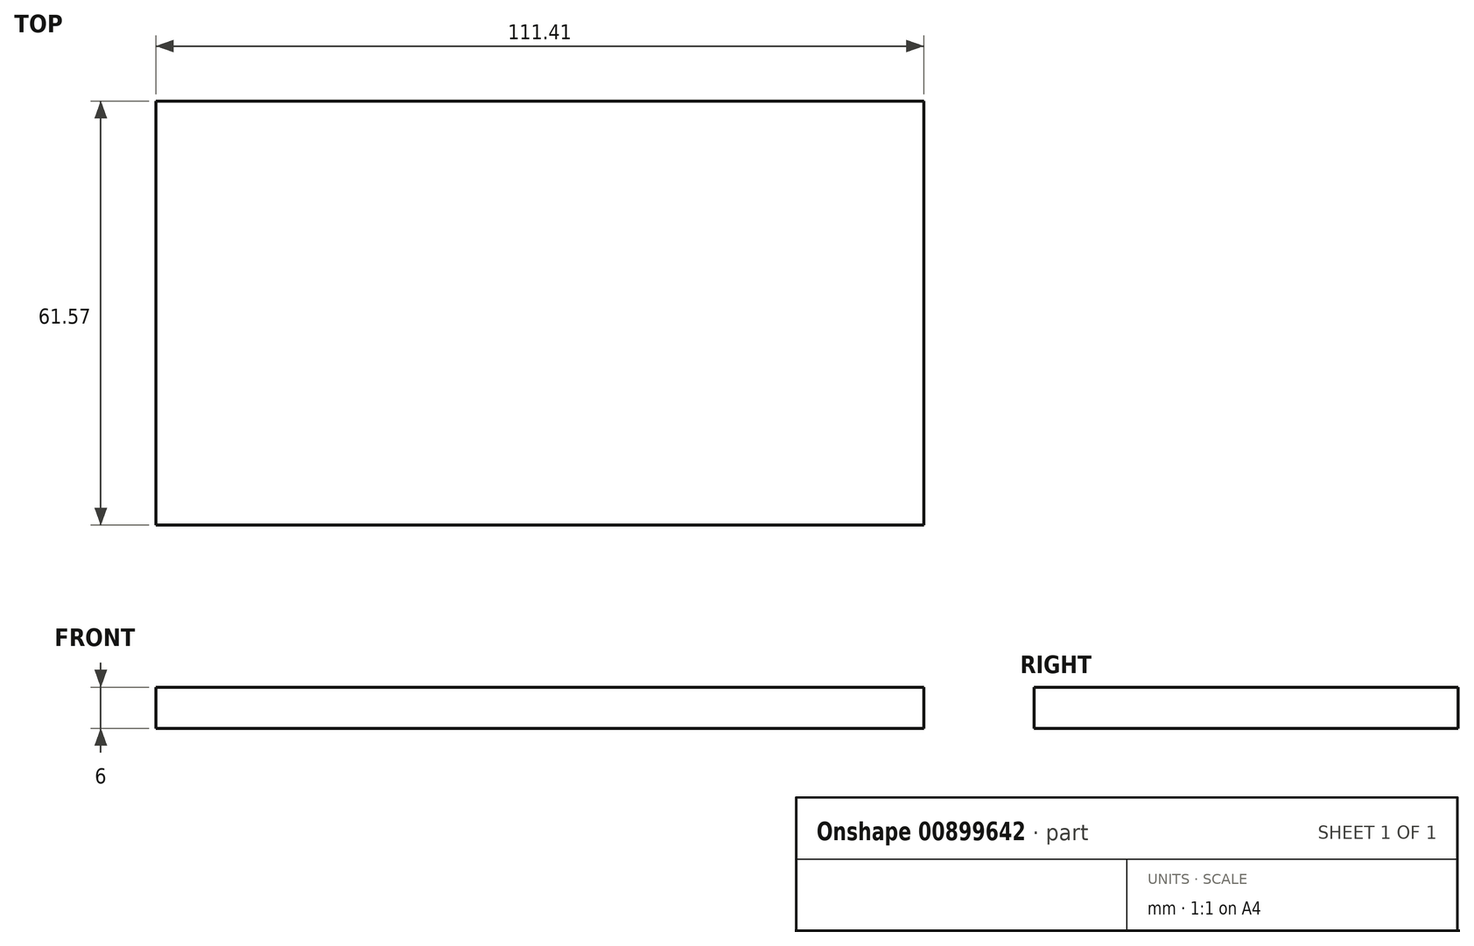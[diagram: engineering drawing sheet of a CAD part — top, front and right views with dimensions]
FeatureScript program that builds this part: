
annotation { "Feature Type Name" : "Feature", "Feature Type Description" : "" }
export const myFeature = defineFeature(function(context is Context, id is Id, definition is map)
    precondition{}
    {
        {
            var Q0;
            Q0=qCreatedBy(makeId("Top.planeOp"),FACE);
            var sketch = newSketch(context, id + "F0", { "sketchPlane" : qUnion([Q0])});
            skLineSegment(sketch, "E0.bottom", {"start": v(-61.04, 8.34) * mm, "end": v(50.37, 8.34) * mm});
            skLineSegment(sketch, "E0.top", {"start": v(-61.04, -53.23) * mm, "end": v(50.37, -53.23) * mm});
            skLineSegment(sketch, "E0.left", {"start": v(-61.04, 8.34) * mm, "end": v(-61.04, -53.23) * mm});
            skLineSegment(sketch, "E0.right", {"start": v(50.37, 8.34) * mm, "end": v(50.37, -53.23) * mm});
            skSolve(sketch);
        }
        {
            var Q0;
            Q0=makeQuery(id+"F0.imprint","IMPRINT",FACE,{"disambiguationData":[TD([[makeQuery(id+"F0.imprint","IMPRINT",EDGE,{"derivedFrom":sQuery(id+"F0.wireOp",EDGE,"E0.bottom")}),-1.0]])]});
            extrude(context, id + "F1", {"entities" : qUnion([Q0]), "depth" : 6 * mm, "offsetDistance" : 25.4 * mm});
        }
    });
